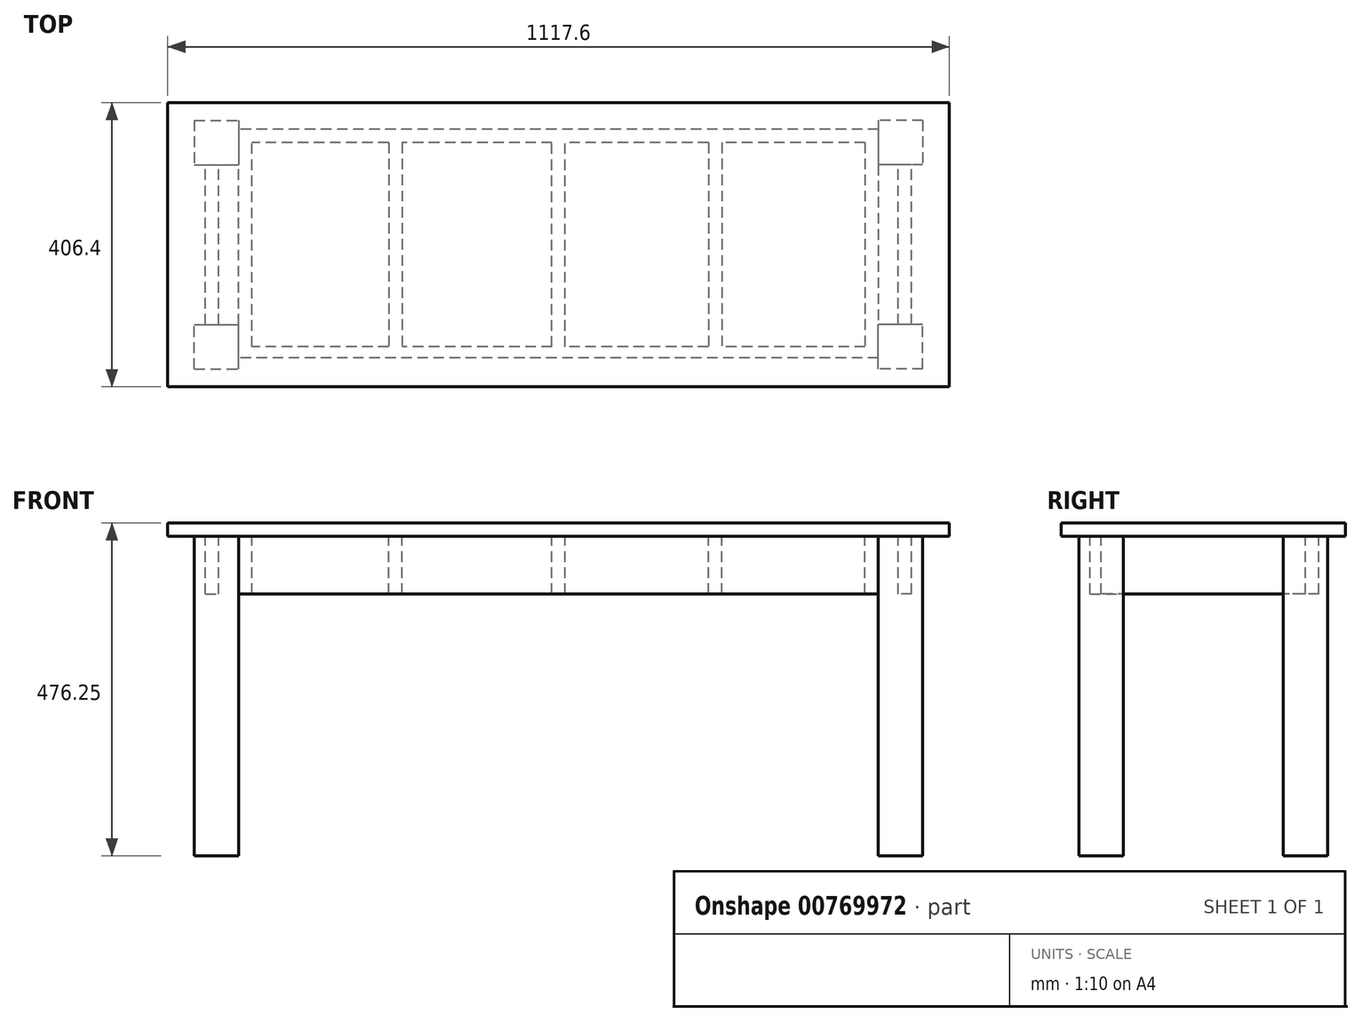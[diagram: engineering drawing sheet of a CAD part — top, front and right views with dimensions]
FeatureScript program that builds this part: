
annotation { "Feature Type Name" : "Feature", "Feature Type Description" : "" }
export const myFeature = defineFeature(function(context is Context, id is Id, definition is map)
    precondition{}
    {
        {
            var Q0;
            Q0=qCreatedBy(makeId("Top.planeOp"),FACE);
            var sketch = newSketch(context, id + "F0", { "sketchPlane" : qUnion([Q0])});
            skLineSegment(sketch, "E0.bottom", {"start": v(558.8, 203.2) * mm, "end": v(-558.8, 203.2) * mm});
            skLineSegment(sketch, "E0.top", {"start": v(558.8, -203.2) * mm, "end": v(-558.8, -203.2) * mm});
            skLineSegment(sketch, "E0.left", {"start": v(558.8, 203.2) * mm, "end": v(558.8, -203.2) * mm});
            skLineSegment(sketch, "E0.right", {"start": v(-558.8, 203.2) * mm, "end": v(-558.8, -203.2) * mm});
            skPoint(sketch, "E0.middle", {"position": v(0, 0) * mm});
            skSolve(sketch);
        }
        {
            var Q0;
            Q0=makeQuery(id+"F0.imprint","IMPRINT",FACE,{"disambiguationData":[TD([[makeQuery(id+"F0.imprint","IMPRINT",EDGE,{"derivedFrom":sQuery(id+"F0.wireOp",EDGE,"E0.bottom")}),1.0]])]});
            extrude(context, id + "F1", {"entities" : qUnion([Q0]), "depth" : 19.05 * mm, "offsetDistance" : 25.4 * mm});
        }
        {
            var Q0;
            Q0=makeQuery(id+"F1.opExtrude","CAP_FACE",FACE,{"disambiguationData":[OSD([sQuery(id+"F0.wireOp",EDGE,"E0.bottom"),sQuery(id+"F0.wireOp",EDGE,"E0.top"),sQuery(id+"F0.wireOp",EDGE,"E0.left"),sQuery(id+"F0.wireOp",EDGE,"E0.right")])],"isStart":true});
            var sketch = newSketch(context, id + "F2", { "sketchPlane" : qUnion([Q0])});
            skLineSegment(sketch, "E1", {"start": v(-558.8, 203.2) * mm, "end": v(-558.8, 177.8) * mm});
            skLineSegment(sketch, "E2", {"start": v(-558.8, 177.8) * mm, "end": v(-520.7, 177.8) * mm});
            skLineSegment(sketch, "E3.bottom", {"start": v(-520.7, 177.8) * mm, "end": v(-457.2, 177.8) * mm});
            skLineSegment(sketch, "E3.top", {"start": v(-520.7, 114.3) * mm, "end": v(-457.2, 114.3) * mm});
            skLineSegment(sketch, "E3.left", {"start": v(-520.7, 177.8) * mm, "end": v(-520.7, 114.3) * mm});
            skLineSegment(sketch, "E3.right", {"start": v(-457.2, 177.8) * mm, "end": v(-457.2, 114.3) * mm});
            skSolve(sketch);
        }
        {
            var Q0;
            Q0=makeQuery(id+"F2.imprint","IMPRINT",FACE,{"disambiguationData":[TD([[makeQuery(id+"F2.imprint","IMPRINT",EDGE,{"derivedFrom":sQuery(id+"F2.wireOp",EDGE,"E3.bottom")}),-1.0]])]});
            extrude(context, id + "F3", {"entities" : qUnion([Q0]), "operationType" : NewBodyOperationType.ADD, "depth" : 457.2 * mm, "offsetDistance" : 25.4 * mm});
        }
        {
            var Q0;
            Q0=makeQuery(id+"F1.opExtrude","SWEPT_BODY",BODY,{"disambiguationData":[OSD([sQuery(id+"F0.wireOp",EDGE,"E0.bottom"),sQuery(id+"F0.wireOp",EDGE,"E0.top"),sQuery(id+"F0.wireOp",EDGE,"E0.left"),sQuery(id+"F0.wireOp",EDGE,"E0.right")])]});
            var Q1;
            Q1=qCreatedBy(makeId("Front.planeOp"),FACE);
            mirror(context, id + "F4", {"operationType" : NewBodyOperationType.ADD, "entities" : qUnion([Q0]), "mirrorPlane" : qUnion([Q1])});
        }
        {
            var Q0;
            Q0=makeQuery(id+"F1.opExtrude","SWEPT_BODY",BODY,{"disambiguationData":[OSD([sQuery(id+"F0.wireOp",EDGE,"E0.bottom"),sQuery(id+"F0.wireOp",EDGE,"E0.top"),sQuery(id+"F0.wireOp",EDGE,"E0.left"),sQuery(id+"F0.wireOp",EDGE,"E0.right")])]});
            var Q1;
            Q1=qCreatedBy(makeId("Right.planeOp"),FACE);
            mirror(context, id + "F5", {"operationType" : NewBodyOperationType.ADD, "entities" : qUnion([Q0]), "mirrorPlane" : qUnion([Q1])});
        }
        {
            var Q0;
            Q0=makeQuery(id+"F1.opExtrude","CAP_FACE",FACE,{"disambiguationData":[OSD([sQuery(id+"F0.wireOp",EDGE,"E0.bottom"),sQuery(id+"F0.wireOp",EDGE,"E0.top"),sQuery(id+"F0.wireOp",EDGE,"E0.left"),sQuery(id+"F0.wireOp",EDGE,"E0.right")])],"isStart":true});
            var sketch = newSketch(context, id + "F6", { "sketchPlane" : qUnion([Q0])});
            skLineSegment(sketch, "E4", {"start": v(520.7, 114.3) * mm, "end": v(504.83, 114.3) * mm});
            skLineSegment(sketch, "E5.bottom", {"start": v(504.83, 114.3) * mm, "end": v(485.78, 114.3) * mm});
            skLineSegment(sketch, "E5.top", {"start": v(504.83, -114.3) * mm, "end": v(485.78, -114.3) * mm});
            skLineSegment(sketch, "E5.left", {"start": v(504.83, 114.3) * mm, "end": v(504.83, -114.3) * mm});
            skLineSegment(sketch, "E5.right", {"start": v(485.78, 114.3) * mm, "end": v(485.78, -114.3) * mm});
            skSolve(sketch);
        }
        {
            var Q0;
            Q0 = qSketchRegion(id + "F6", true);
            extrude(context, id + "F7", {"entities" : qUnion([Q0]), "operationType" : NewBodyOperationType.ADD, "depth" : 82.55 * mm, "offsetDistance" : 25.4 * mm});
        }
        {
            var Q0;
            Q0=makeQuery(id+"F1.opExtrude","SWEPT_BODY",BODY,{"disambiguationData":[OSD([sQuery(id+"F0.wireOp",EDGE,"E0.bottom"),sQuery(id+"F0.wireOp",EDGE,"E0.top"),sQuery(id+"F0.wireOp",EDGE,"E0.left"),sQuery(id+"F0.wireOp",EDGE,"E0.right")])]});
            var Q1;
            Q1=qCreatedBy(makeId("Right.planeOp"),FACE);
            mirror(context, id + "F8", {"operationType" : NewBodyOperationType.ADD, "entities" : qUnion([Q0]), "mirrorPlane" : qUnion([Q1])});
        }
        {
            var Q0;
            Q0=makeQuery(id+"F1.opExtrude","CAP_FACE",FACE,{"disambiguationData":[OSD([sQuery(id+"F0.wireOp",EDGE,"E0.bottom"),sQuery(id+"F0.wireOp",EDGE,"E0.top"),sQuery(id+"F0.wireOp",EDGE,"E0.left"),sQuery(id+"F0.wireOp",EDGE,"E0.right")])],"isStart":true});
            var sketch = newSketch(context, id + "F9", { "sketchPlane" : qUnion([Q0])});
            skLineSegment(sketch, "E6", {"start": v(457.2, -177.8) * mm, "end": v(457.2, -165.1) * mm});
            skLineSegment(sketch, "E7", {"start": v(457.2, -165.1) * mm, "end": v(457.2, -177.8) * mm});
            skLineSegment(sketch, "E8.bottom", {"start": v(457.2, -165.1) * mm, "end": v(-457.2, -165.1) * mm});
            skLineSegment(sketch, "E8.top", {"start": v(457.2, -146.05) * mm, "end": v(-457.2, -146.05) * mm});
            skLineSegment(sketch, "E8.left", {"start": v(457.2, -165.1) * mm, "end": v(457.2, -146.05) * mm});
            skLineSegment(sketch, "E8.right", {"start": v(-457.2, -165.1) * mm, "end": v(-457.2, -146.05) * mm});
            skSolve(sketch);
        }
        {
            var Q0;
            Q0 = qSketchRegion(id + "F9", true);
            extrude(context, id + "F10", {"entities" : qUnion([Q0]), "operationType" : NewBodyOperationType.ADD, "depth" : 82.55 * mm, "offsetDistance" : 25.4 * mm});
        }
        {
            var Q0;
            Q0=makeQuery(id+"F1.opExtrude","CAP_FACE",FACE,{"disambiguationData":[OSD([sQuery(id+"F0.wireOp",EDGE,"E0.bottom"),sQuery(id+"F0.wireOp",EDGE,"E0.top"),sQuery(id+"F0.wireOp",EDGE,"E0.left"),sQuery(id+"F0.wireOp",EDGE,"E0.right")])],"isStart":true});
            var sketch = newSketch(context, id + "F11", { "sketchPlane" : qUnion([Q0])});
            skLineSegment(sketch, "E9", {"start": v(457.2, 177.8) * mm, "end": v(457.2, 161.93) * mm});
            skLineSegment(sketch, "E10.bottom", {"start": v(457.2, 161.93) * mm, "end": v(-457.2, 161.93) * mm});
            skLineSegment(sketch, "E10.top", {"start": v(457.2, 146.05) * mm, "end": v(-457.2, 146.05) * mm});
            skLineSegment(sketch, "E10.left", {"start": v(457.2, 161.93) * mm, "end": v(457.2, 146.05) * mm});
            skLineSegment(sketch, "E10.right", {"start": v(-457.2, 161.93) * mm, "end": v(-457.2, 146.05) * mm});
            skSolve(sketch);
        }
        {
            var Q0;
            Q0 = qSketchRegion(id + "F11", true);
            extrude(context, id + "F12", {"entities" : qUnion([Q0]), "operationType" : NewBodyOperationType.ADD, "depth" : 82.55 * mm, "offsetDistance" : 25.4 * mm});
        }
        {
            var Q0;
            Q0=makeQuery(id+"F5.opPattern","COPY",FACE,{"derivedFrom":makeQuery(id+"F4.opPattern","COPY",FACE,{"derivedFrom":makeQuery(id+"F3.opExtrude","SWEPT_FACE",FACE,{"disambiguationData":[OSD([sQuery(id+"F2.wireOp",EDGE,"E3.right")])]}),"instanceName":"1"}),"instanceName":"1"});
            var sketch = newSketch(context, id + "F13", { "sketchPlane" : qUnion([Q0])});
            skLineSegment(sketch, "E11.bottom", {"start": v(-146.05, -82.55) * mm, "end": v(146.12, -82.55) * mm});
            skLineSegment(sketch, "E11.top", {"start": v(-146.05, 0) * mm, "end": v(146.12, 0) * mm});
            skLineSegment(sketch, "E11.left", {"start": v(-146.05, -82.55) * mm, "end": v(-146.05, 0) * mm});
            skLineSegment(sketch, "E11.right", {"start": v(146.12, -82.55) * mm, "end": v(146.12, 0) * mm});
            skSolve(sketch);
        }
        {
            var Q0;
            Q0 = qSketchRegion(id + "F13", true);
            extrude(context, id + "F14", {"entities" : qUnion([Q0]), "operationType" : NewBodyOperationType.ADD, "depth" : 19.05 * mm, "offsetDistance" : 25.4 * mm});
        }
        {
            var Q0;
            Q0=makeQuery(id+"F3.opExtrude","SWEPT_FACE",FACE,{"disambiguationData":[OSD([sQuery(id+"F2.wireOp",EDGE,"E3.right")])]});
            var sketch = newSketch(context, id + "F15", { "sketchPlane" : qUnion([Q0])});
            skLineSegment(sketch, "E12.bottom", {"start": v(-146.05, -82.55) * mm, "end": v(146.26, -82.55) * mm});
            skLineSegment(sketch, "E12.top", {"start": v(-146.05, 0) * mm, "end": v(146.26, 0) * mm});
            skLineSegment(sketch, "E12.left", {"start": v(-146.05, -82.55) * mm, "end": v(-146.05, 0) * mm});
            skLineSegment(sketch, "E12.right", {"start": v(146.26, -82.55) * mm, "end": v(146.26, 0) * mm});
            skSolve(sketch);
        }
        {
            var Q0;
            Q0 = qSketchRegion(id + "F15", true);
            extrude(context, id + "F16", {"entities" : qUnion([Q0]), "operationType" : NewBodyOperationType.ADD, "depth" : 19.05 * mm, "offsetDistance" : 25.4 * mm});
        }
        {
            var Q0;
            {var subQ0=makeQuery(id+"F10.opExtrude","SWEPT_FACE",FACE,{"disambiguationData":[OSD([sQuery(id+"F9.wireOp",EDGE,"E8.top")])]});var subQ5=makeQuery(id+"F3.opExtrude","SWEPT_FACE",FACE,{"disambiguationData":[OSD([sQuery(id+"F2.wireOp",EDGE,"E3.top")])]});var subQ7=makeQuery(id+"F7.opExtrude","SWEPT_FACE",FACE,{"disambiguationData":[OSD([sQuery(id+"F6.wireOp",EDGE,"E5.right")])]});Q0=makeQuery(id+"F16.boolean.opBoolean","SPLIT",FACE,{"disambiguationData":[TD([subQ0])],"derivedFrom":makeQuery(id+"F14.boolean.opBoolean","SPLIT",FACE,{"disambiguationData":[TD([subQ5])],"derivedFrom":makeQuery(id+"F12.boolean.opBoolean","SPLIT",FACE,{"disambiguationData":[TD([subQ7])],"derivedFrom":makeQuery(id+"F1.opExtrude","CAP_FACE",FACE,{"disambiguationData":[OSD([sQuery(id+"F0.wireOp",EDGE,"E0.bottom"),sQuery(id+"F0.wireOp",EDGE,"E0.top"),sQuery(id+"F0.wireOp",EDGE,"E0.left"),sQuery(id+"F0.wireOp",EDGE,"E0.right")])],"isStart":true})})})});}
            var sketch = newSketch(context, id + "F17", { "sketchPlane" : qUnion([Q0])});
            skLineSegment(sketch, "E13.bottom", {"start": v(9.53, 146.05) * mm, "end": v(-9.53, 146.05) * mm});
            skLineSegment(sketch, "E13.top", {"start": v(9.53, -146.05) * mm, "end": v(-9.53, -146.05) * mm});
            skLineSegment(sketch, "E13.left", {"start": v(9.53, 146.05) * mm, "end": v(9.53, -146.05) * mm});
            skLineSegment(sketch, "E13.right", {"start": v(-9.53, 146.05) * mm, "end": v(-9.53, -146.05) * mm});
            skPoint(sketch, "E13.middle", {"position": v(0, 0) * mm});
            skSolve(sketch);
        }
        {
            var Q0;
            Q0 = qSketchRegion(id + "F17", true);
            extrude(context, id + "F18", {"entities" : qUnion([Q0]), "operationType" : NewBodyOperationType.ADD, "depth" : 82.55 * mm, "offsetDistance" : 25.4 * mm});
        }
        {
            var Q0;
            {var subQ0=makeQuery(id+"F10.opExtrude","SWEPT_FACE",FACE,{"disambiguationData":[OSD([sQuery(id+"F9.wireOp",EDGE,"E8.top")])]});var subQ6=makeQuery(id+"F3.opExtrude","SWEPT_FACE",FACE,{"disambiguationData":[OSD([sQuery(id+"F2.wireOp",EDGE,"E3.top")])]});var subQ8=makeQuery(id+"F7.opExtrude","SWEPT_FACE",FACE,{"disambiguationData":[OSD([sQuery(id+"F6.wireOp",EDGE,"E5.right")])]});Q0=makeQuery(id+"F18.boolean.opBoolean","SPLIT",FACE,{"disambiguationData":[TD([makeQuery(id+"F18.opExtrude","SWEPT_FACE",FACE,{"disambiguationData":[OSD([sQuery(id+"F17.wireOp",EDGE,"E13.right")])]})])],"derivedFrom":makeQuery(id+"F16.boolean.opBoolean","SPLIT",FACE,{"disambiguationData":[TD([subQ0])],"derivedFrom":makeQuery(id+"F14.boolean.opBoolean","SPLIT",FACE,{"disambiguationData":[TD([subQ6])],"derivedFrom":makeQuery(id+"F12.boolean.opBoolean","SPLIT",FACE,{"disambiguationData":[TD([subQ8])],"derivedFrom":makeQuery(id+"F1.opExtrude","CAP_FACE",FACE,{"disambiguationData":[OSD([sQuery(id+"F0.wireOp",EDGE,"E0.bottom"),sQuery(id+"F0.wireOp",EDGE,"E0.top"),sQuery(id+"F0.wireOp",EDGE,"E0.left"),sQuery(id+"F0.wireOp",EDGE,"E0.right")])],"isStart":true})})})})});}
            var sketch = newSketch(context, id + "F19", { "sketchPlane" : qUnion([Q0])});
            skLineSegment(sketch, "E14.bottom", {"start": v(-223.84, -146.05) * mm, "end": v(-242.89, -146.05) * mm});
            skLineSegment(sketch, "E14.top", {"start": v(-223.84, 438.15) * mm, "end": v(-242.89, 438.15) * mm});
            skLineSegment(sketch, "E14.left", {"start": v(-223.84, -146.05) * mm, "end": v(-223.84, 438.15) * mm});
            skLineSegment(sketch, "E14.right", {"start": v(-242.89, -146.05) * mm, "end": v(-242.89, 438.15) * mm});
            skPoint(sketch, "E14.middle", {"position": v(-233.36, 146.05) * mm});
            skLineSegment(sketch, "E15.bottom", {"start": v(-242.89, 146.05) * mm, "end": v(-223.84, 146.05) * mm});
            skLineSegment(sketch, "E15.top", {"start": v(-242.89, -146.05) * mm, "end": v(-223.84, -146.05) * mm});
            skLineSegment(sketch, "E15.left", {"start": v(-242.89, 146.05) * mm, "end": v(-242.89, -146.05) * mm});
            skLineSegment(sketch, "E15.right", {"start": v(-223.84, 146.05) * mm, "end": v(-223.84, -146.05) * mm});
            skSolve(sketch);
        }
        {
            var Q0;
            Q0=makeQuery(id+"F19.imprint","IMPRINT",FACE,{"disambiguationData":[TD([[makeQuery(id+"F19.imprint","IMPRINT",EDGE,{"derivedFrom":sQuery(id+"F19.wireOp",EDGE,"E15.bottom")}),1.0]])]});
            extrude(context, id + "F20", {"entities" : qUnion([Q0]), "operationType" : NewBodyOperationType.ADD, "depth" : 82.55 * mm, "offsetDistance" : 25.4 * mm});
        }
        {
            var Q0;
            {var subQ0=makeQuery(id+"F10.opExtrude","SWEPT_FACE",FACE,{"disambiguationData":[OSD([sQuery(id+"F9.wireOp",EDGE,"E8.top")])]});var subQ5=makeQuery(id+"F3.opExtrude","SWEPT_FACE",FACE,{"disambiguationData":[OSD([sQuery(id+"F2.wireOp",EDGE,"E3.top")])]});var subQ7=makeQuery(id+"F7.opExtrude","SWEPT_FACE",FACE,{"disambiguationData":[OSD([sQuery(id+"F6.wireOp",EDGE,"E5.right")])]});Q0=makeQuery(id+"F18.boolean.opBoolean","SPLIT",FACE,{"disambiguationData":[TD([makeQuery(id+"F18.opExtrude","SWEPT_FACE",FACE,{"disambiguationData":[OSD([sQuery(id+"F17.wireOp",EDGE,"E13.left")])]})])],"derivedFrom":makeQuery(id+"F16.boolean.opBoolean","SPLIT",FACE,{"disambiguationData":[TD([subQ0])],"derivedFrom":makeQuery(id+"F14.boolean.opBoolean","SPLIT",FACE,{"disambiguationData":[TD([subQ5])],"derivedFrom":makeQuery(id+"F12.boolean.opBoolean","SPLIT",FACE,{"disambiguationData":[TD([subQ7])],"derivedFrom":makeQuery(id+"F1.opExtrude","CAP_FACE",FACE,{"disambiguationData":[OSD([sQuery(id+"F0.wireOp",EDGE,"E0.bottom"),sQuery(id+"F0.wireOp",EDGE,"E0.top"),sQuery(id+"F0.wireOp",EDGE,"E0.left"),sQuery(id+"F0.wireOp",EDGE,"E0.right")])],"isStart":true})})})})});}
            var sketch = newSketch(context, id + "F21", { "sketchPlane" : qUnion([Q0])});
            skLineSegment(sketch, "E16.bottom", {"start": v(233.36, -146.05) * mm, "end": v(214.31, -146.05) * mm});
            skLineSegment(sketch, "E16.top", {"start": v(233.36, 438.15) * mm, "end": v(214.31, 438.15) * mm});
            skLineSegment(sketch, "E16.left", {"start": v(233.36, -146.05) * mm, "end": v(233.36, 438.15) * mm});
            skLineSegment(sketch, "E16.right", {"start": v(214.31, -146.05) * mm, "end": v(214.31, 438.15) * mm});
            skPoint(sketch, "E16.middle", {"position": v(223.84, 146.05) * mm});
            skLineSegment(sketch, "E17.bottom", {"start": v(214.31, 146.05) * mm, "end": v(233.36, 146.05) * mm});
            skLineSegment(sketch, "E17.top", {"start": v(214.31, -146.05) * mm, "end": v(233.36, -146.05) * mm});
            skLineSegment(sketch, "E17.left", {"start": v(214.31, 146.05) * mm, "end": v(214.31, -146.05) * mm});
            skLineSegment(sketch, "E17.right", {"start": v(233.36, 146.05) * mm, "end": v(233.36, -146.05) * mm});
            skSolve(sketch);
        }
        {
            var Q0;
            Q0=makeQuery(id+"F21.imprint","IMPRINT",FACE,{"disambiguationData":[TD([[makeQuery(id+"F21.imprint","IMPRINT",EDGE,{"derivedFrom":sQuery(id+"F21.wireOp",EDGE,"E17.bottom")}),1.0]])]});
            extrude(context, id + "F22", {"entities" : qUnion([Q0]), "operationType" : NewBodyOperationType.ADD, "depth" : 82.55 * mm, "offsetDistance" : 25.4 * mm});
        }
    });
